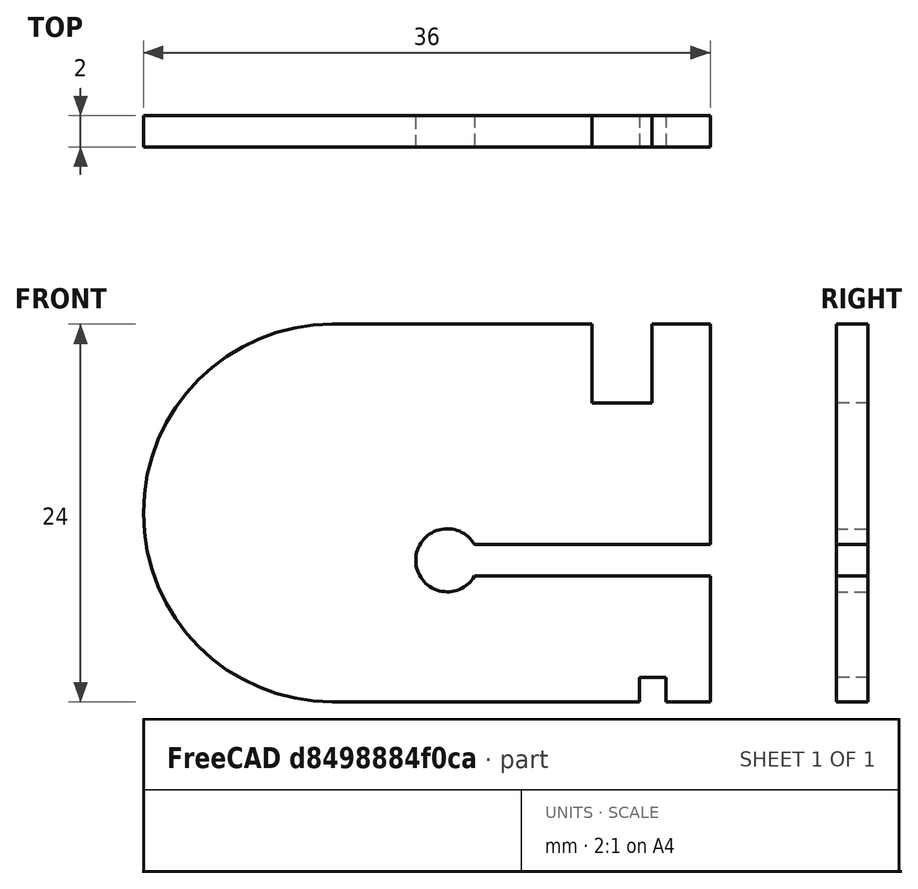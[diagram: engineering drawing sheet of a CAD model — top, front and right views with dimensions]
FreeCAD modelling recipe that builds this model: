
FCSTD DOCUMENT  (FreeCAD 1.0R)
Label: CW-Pad-Middle-Dah
License: All rights reserved
LicenseURL: https://en.wikipedia.org/wiki/All_rights_reserved
objects: Sketcher::SketchObject×1, PartDesign::Pad×1, PartDesign::Body×1, Part::Part2DObjectPython×1
note: 7 computed .brp shape members not serialized (recipe doc carries the construction recipe); baked Part::Feature solids carry a one-line shape summary decoded from their .brp

FEATURE [Sketcher::SketchObject] Sketch
  ArcFitTolerance = 1e-06
  AttachmentSupport = -> [XZ_Plane]
  FullyConstrained = true
  MakeInternals = false
  MapMode = 5
  Placement = pos=(0,0,0) rot=(1,0,0;1.5708rad)
  sketch-geometry (24):
    g0: GeomPoint [constr] X=0 Y=0 Z=0
    g1: GeomPoint [constr] X=0 Y=0 Z=0
    g2: LineSegment StartX=-15 StartY=-12 StartZ=0 EndX=4.5 EndY=-12 EndZ=0
    g3: LineSegment StartX=9 StartY=12 StartZ=0 EndX=5.3 EndY=12 EndZ=0
    g4: GeomPoint [constr] X=-3 Y=0 Z=0
    g5: ArcOfCircle CenterX=-15 CenterY=1e-16 CenterZ=0 NormalX=0 NormalY=0 NormalZ=1 AngleXU=0 Radius=12 StartAngle=1.5708 EndAngle=4.71239
    g6: LineSegment StartX=6.2 StartY=-12 StartZ=0 EndX=6.2 EndY=-10.45 EndZ=0
    g7: LineSegment StartX=6.2 StartY=-10.45 StartZ=0 EndX=4.5 EndY=-10.45 EndZ=0
    g8: LineSegment StartX=4.5 StartY=-10.45 StartZ=0 EndX=4.5 EndY=-12 EndZ=0
    g9: GeomPoint [constr] X=5.35 Y=-11.225 Z=0
    g10: LineSegment StartX=6.2 StartY=-12 StartZ=0 EndX=9 EndY=-12 EndZ=0
    g11: LineSegment StartX=1.5 StartY=7 StartZ=0 EndX=5.3 EndY=7 EndZ=0
    g12: LineSegment StartX=5.3 StartY=7 StartZ=0 EndX=5.3 EndY=12 EndZ=0
    g13: LineSegment StartX=1.5 StartY=12 StartZ=0 EndX=1.5 EndY=7 EndZ=0
    g14: GeomPoint [constr] X=3.4 Y=9.5 Z=0
    g15: LineSegment StartX=1.5 StartY=12 StartZ=0 EndX=-15 EndY=12 EndZ=0
    g16: Circle [constr] CenterX=-15 CenterY=1e-16 CenterZ=0 NormalX=0 NormalY=0 NormalZ=1 AngleXU=0 Radius=9.875
    g17: LineSegment [constr] StartX=1.5 StartY=30 StartZ=0 EndX=1.5 EndY=-30 EndZ=0
    g18: LineSegment StartX=-5.9714 StartY=-4 StartZ=0 EndX=9 EndY=-4 EndZ=0
    g19: LineSegment StartX=9 StartY=-2 StartZ=0 EndX=-5.9714 EndY=-2 EndZ=0
    g20: GeomPoint [constr] X=1.5143 Y=-3 Z=0
    g21: LineSegment StartX=9 StartY=-12 StartZ=0 EndX=9 EndY=-4 EndZ=0
    g22: LineSegment StartX=9 StartY=12 StartZ=0 EndX=9 EndY=-2 EndZ=0
    g23: ArcOfCircle CenterX=-7.70345 CenterY=-3 CenterZ=0 NormalX=0 NormalY=0 NormalZ=1 AngleXU=0 Radius=2 StartAngle=0.523599 EndAngle=5.75959
  constraints (61):
    c: Coincident(g0,g-1)
    c: Coincident(g1,g0)
    c: Horizontal(g2)
    c: Horizontal(g3)
    c: Symmetric(g3,g2,g4)
    c: Distance(g2,g15) = 24
    c: Horizontal(g4,g0)
    c: Coincident(g5,g2)
    c: Coincident(g5,g15)
    c: DistanceX(g5,g0) = 15
    c: Coincident(g6,g7)
    c: Coincident(g7,g8)
    c: Horizontal(g7)
    c: Vertical(g6)
    c: Vertical(g8)
    c: Symmetric(g7,g8,g9)
    c: DistanceX(g0,g8) = 4.5
    c: Equal(g8,g6)
    c: Parallel(g10,g2)
    c: Coincident(g6,g10)
    c: Coincident(g8,g2)
    c: Coincident(g11,g12)
    c: Coincident(g13,g11)
    c: Horizontal(g11)
    c: Vertical(g12)
    c: Vertical(g13)
    c: Symmetric(g12,g11,g14)
    c: DistanceX(g0,g13) = 1.5
    c: Coincident(g15,g13)
    c: Parallel(g15,g2)
    c: DistanceX(g13,g3) = 3.8
    c: Diameter(g16) = 19.75
    c: Coincident(g16,g5)
    c: DistanceY(g17,g17) = 60
    c: DistanceX(g0,g17) = 1.5
    c: Symmetric(g17,g17,g-1)
    c: DistanceY(g2,g7) = 1.55
    c: DistanceX(g2,g6) = 1.7
    c: Symmetric(g5,g2,g-1)
    c: DistanceX(g0,g3) = 9
    c: Coincident(g12,g3)
    c: DistanceY(g11,g3) = 5
    c: Vertical(g5,g5)
    c: Horizontal(g18)
    c: Horizontal(g19)
    c: Symmetric(g18,g19,g20)
    c: DistanceY(g-1,g20) = -3
    c: Vertical(g3,g19)
    c: Coincident(g21,g10)
    c: Coincident(g21,g18)
    c: Vertical(g21)
    c: Coincident(g22,g3)
    c: Coincident(g22,g19)
    c: Vertical(g3,g10)
    c: DistanceY(g18,g19) = 2
    c: Vertical(g19,g18)
    c: Horizontal(g23,g20)
    c: Diameter(g23) = 4
    c: Coincident(g23,g18)
    c: Vertical(g23,g19)
    c: PointOnObject(g18,g16)
FEATURE [PartDesign::Pad] Pad
  Direction = (0,-1,2e-16)
  Length = 2
  Length2 = 10
  Midplane = true
  Placement = pos=(0,0,0) rot=(1,0,0;1.5708rad)
  Profile = -> Sketch
  ReferenceAxis = -> Sketch [N_Axis]
  Refine = true
  Suppressed = false
  Type = 0
FEATURE [PartDesign::Body] Body  label="CW-Pad-Middle-Dah"
  AllowCompound = false
  Group = -> [Sketch,Pad]
  Origin = -> Origin
  Tip = -> Pad
FEATURE [Part::Part2DObjectPython] Shape2DView  # Draft 2D object (typed FeaturePython)
  AutoUpdate = true
  Base = -> Pad
  Clip = false
  FuseArch = false
  HiddenLines = false
  InPlace = true
  OnlySolids = false
  Projection = (0,-1,0)
  ProjectionMode = 0
  SegmentLength = 0.05
  Tessellation = false
  VisibleOnly = false
